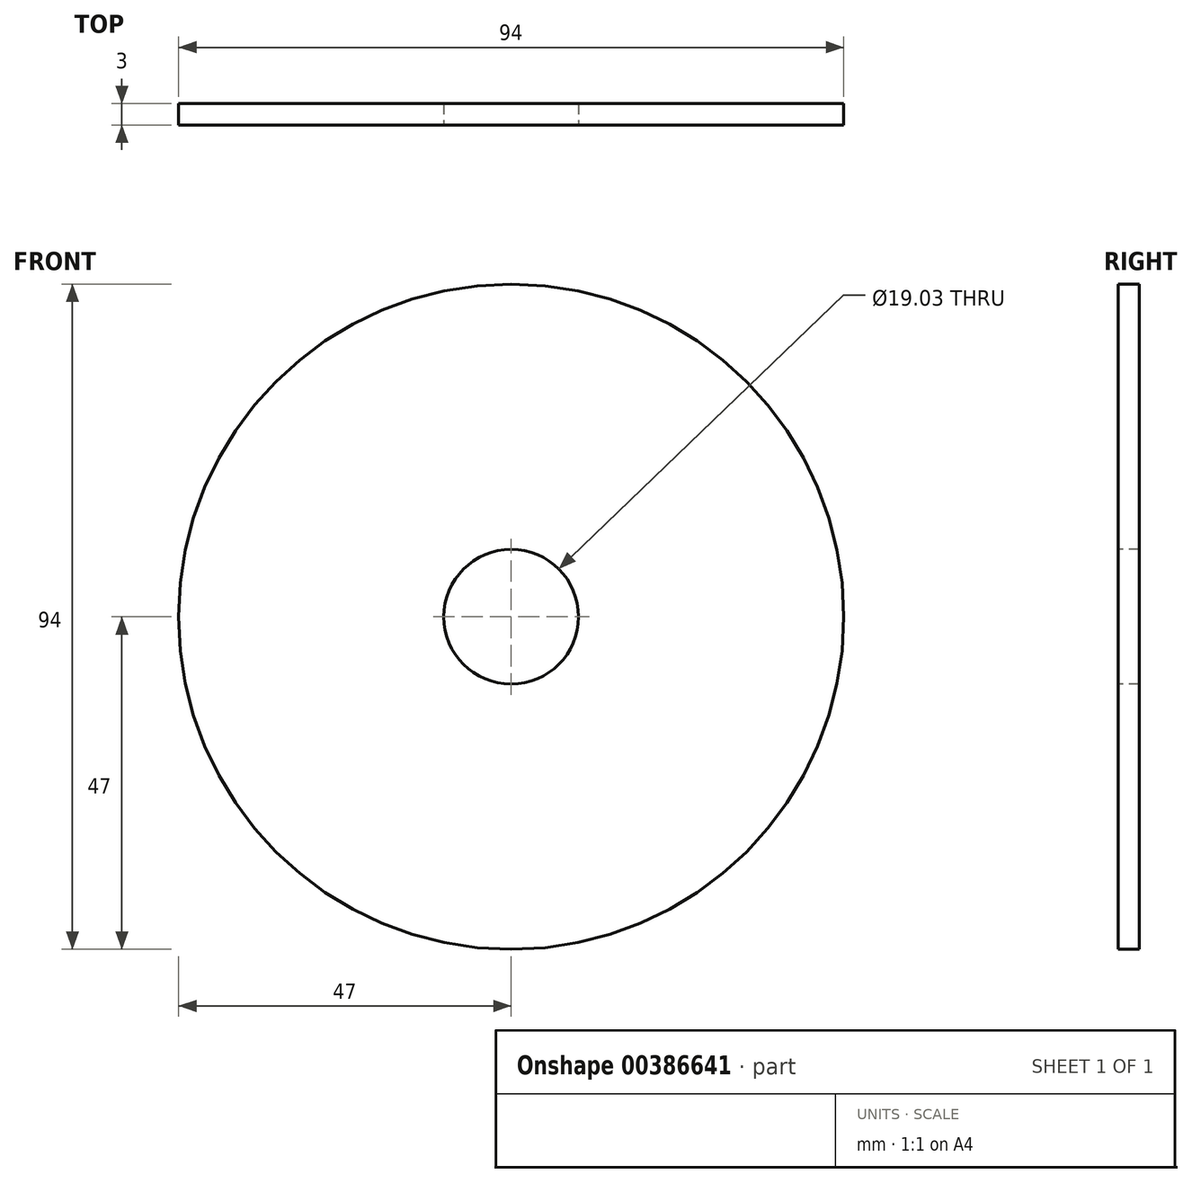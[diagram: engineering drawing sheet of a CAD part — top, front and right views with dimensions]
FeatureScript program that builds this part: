
annotation { "Feature Type Name" : "Feature", "Feature Type Description" : "" }
export const myFeature = defineFeature(function(context is Context, id is Id, definition is map)
    precondition{}
    {
        {
            var Q0;
            Q0=qCreatedBy(makeId("Front.planeOp"),FACE);
            var sketch = newSketch(context, id + "F0", { "sketchPlane" : qUnion([Q0])});
            skCircle(sketch, "E0", {"center": v(0, 0) * mm, "radius": 47 * mm});
            skCircle(sketch, "E1", {"center": v(0, 0) * mm, "radius": 9.52 * mm});
            skSolve(sketch);
        }
        {
            var Q0;
            Q0 = qSketchRegion(id + "F0", true);
            extrude(context, id + "F1", {"entities" : qUnion([Q0]), "oppositeDirection" : true, "depth" : 3 * mm});
        }
    });
